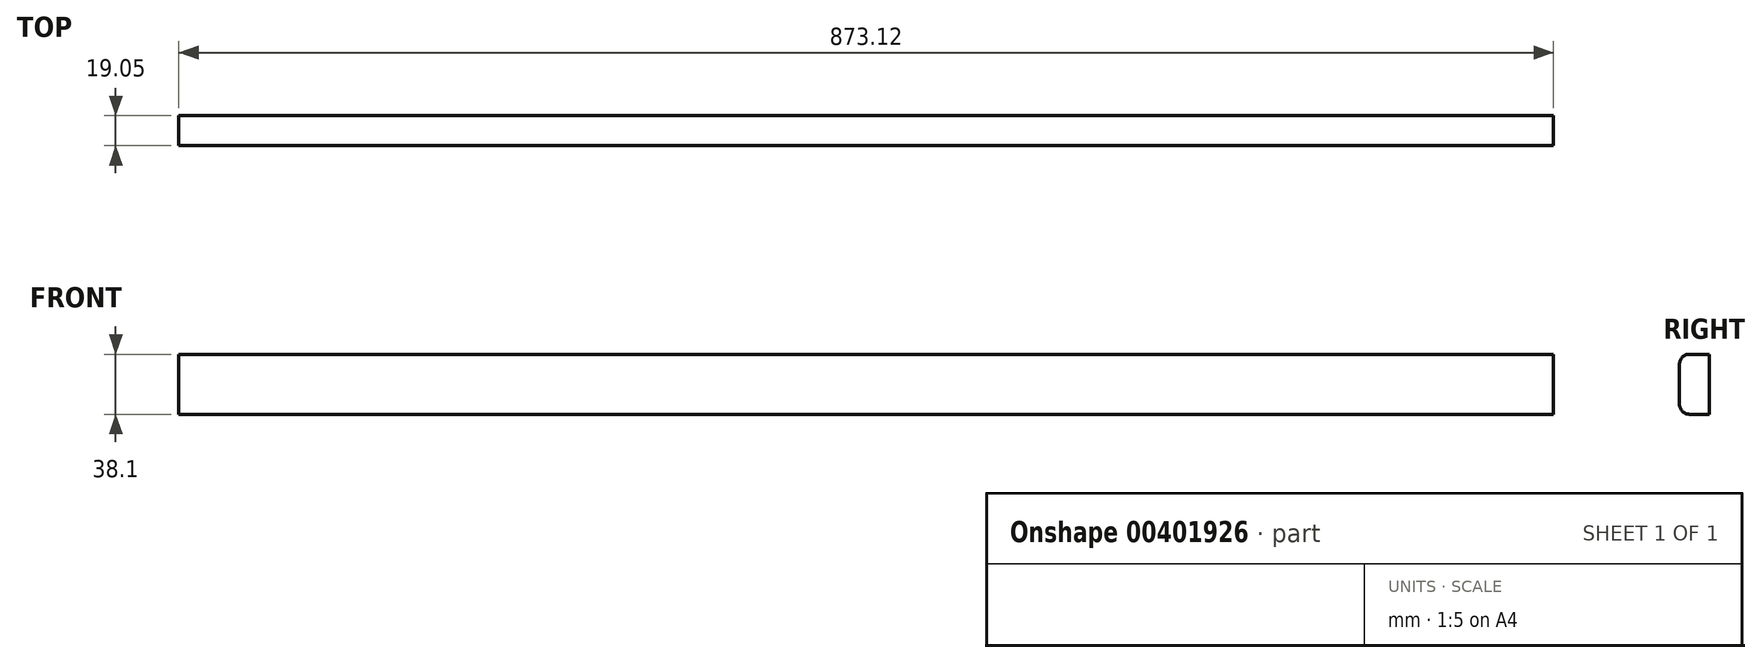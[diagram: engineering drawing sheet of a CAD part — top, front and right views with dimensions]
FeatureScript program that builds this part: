
annotation { "Feature Type Name" : "Feature", "Feature Type Description" : "" }
export const myFeature = defineFeature(function(context is Context, id is Id, definition is map)
    precondition{}
    {
        {
            var Q0;
            Q0=qCreatedBy(makeId("Front.planeOp"),FACE);
            var sketch = newSketch(context, id + "F0", { "sketchPlane" : qUnion([Q0])});
            skLineSegment(sketch, "E0.bottom", {"start": v(436.56, -19.05) * mm, "end": v(-436.56, -19.05) * mm});
            skLineSegment(sketch, "E0.top", {"start": v(436.56, 19.05) * mm, "end": v(-436.56, 19.05) * mm});
            skLineSegment(sketch, "E0.left", {"start": v(436.56, -19.05) * mm, "end": v(436.56, 19.05) * mm});
            skLineSegment(sketch, "E0.right", {"start": v(-436.56, -19.05) * mm, "end": v(-436.56, 19.05) * mm});
            skPoint(sketch, "E0.middle", {"position": v(0, 0) * mm});
            skSolve(sketch);
        }
        {
            var Q0;
            Q0=qSketchRegion(id+"F0",true);
            extrude(context, id + "F1", {"entities" : qUnion([Q0]), "depth" : 19.05 * mm});
        }
        {
            var Q0;
            Q0=makeQuery(id+"F1.opExtrude","CAP_EDGE",EDGE,{"disambiguationData":[OSD([sQuery(id+"F0.wireOp",EDGE,"E0.top")])],"isStart":false});
            var Q1;
            Q1=makeQuery(id+"F1.opExtrude","CAP_EDGE",EDGE,{"disambiguationData":[OSD([sQuery(id+"F0.wireOp",EDGE,"E0.bottom")])],"isStart":false});
            fillet(context, id + "F2", {"entities" : qUnion([Q0, Q1]), "radius" : 6.35 * mm, "tangentPropagation" : true, "allowEdgeOverflow" : false});
        }
    });
